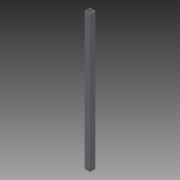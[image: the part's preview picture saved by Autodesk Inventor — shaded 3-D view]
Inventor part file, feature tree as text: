
AUTODESK INVENTOR PART (.ipt)
format: ipt  version: 2013 (Build 170138000, 138)  size: 72,704 bytes
history: native  units: in
note: dims shown in document units (in); Inventor stores cm internally (conversion verified against a paired STEP export)
features: extrude x1, sketch x1
ambient origin geometry x8: Origin, YZ Plane, XZ Plane, XY Plane, X Axis, Y Axis, Z Axis, Center Point
bodies: Solid1 (feature_tree)
feature tree (2):
  extrude  "Extrusion1"  Depth=1.0in
  sketch  "Sketch1"  dims[d0=1.0in d2=1.0in d3=0.0625in d4=26.375in d5=0.0in]
